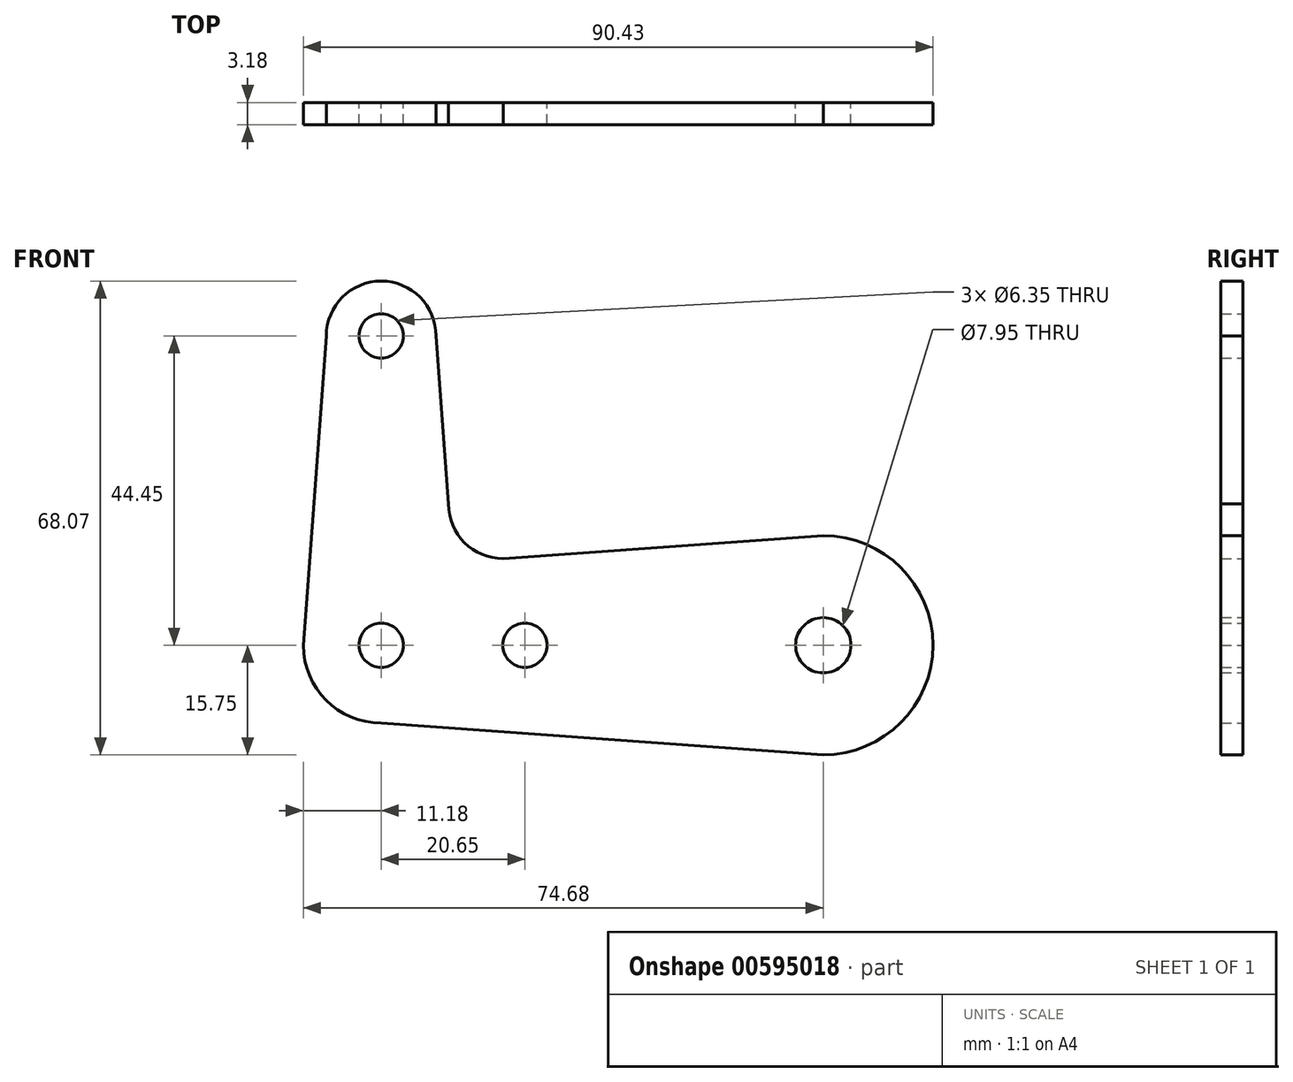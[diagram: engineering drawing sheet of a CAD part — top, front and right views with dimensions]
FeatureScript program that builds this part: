
annotation { "Feature Type Name" : "Feature", "Feature Type Description" : "" }
export const myFeature = defineFeature(function(context is Context, id is Id, definition is map)
    precondition{}
    {
        {
            var Q0;
            Q0=qCreatedBy(makeId("Front.planeOp"),FACE);
            var sketch = newSketch(context, id + "F0", { "sketchPlane" : qUnion([Q0])});
            skLineSegment(sketch, "E0", {"start": v(-20.65, 0) * mm, "end": v(42.85, 0) * mm, "construction": true});
            skLineSegment(sketch, "E1", {"start": v(-20.65, 44.45) * mm, "end": v(-20.65, 0) * mm, "construction": true});
            skCircle(sketch, "E2", {"center": v(-20.65, 0) * mm, "radius": 3.18 * mm});
            skCircle(sketch, "E3", {"center": v(0, 0) * mm, "radius": 3.18 * mm});
            skCircle(sketch, "E4", {"center": v(42.85, 0) * mm, "radius": 3.98 * mm});
            skCircle(sketch, "E5", {"center": v(-20.65, 44.45) * mm, "radius": 3.18 * mm});
            skLineSegment(sketch, "E6", {"start": v(-28.52, 44.45) * mm, "end": v(-31.83, 0) * mm});
            skArc(sketch, "E7", {"start": v(-12.78, 44.45) * mm, "mid": v(-20.65, 52.32) * mm, "end": v(-28.52, 44.45) * mm});
            skArc(sketch, "E8", {"start": v(42.85, -15.75) * mm, "mid": v(58.6, 0) * mm, "end": v(42.85, 15.75) * mm});
            skArc(sketch, "E9", {"start": v(-31.83, 0) * mm, "mid": v(-28.55, -7.9) * mm, "end": v(-20.65, -11.18) * mm});
            skLineSegment(sketch, "E10", {"start": v(-20.65, -11.18) * mm, "end": v(42.85, -15.75) * mm});
            skLineSegment(sketch, "E11", {"start": v(-12.78, 44.45) * mm, "end": v(-10.98, 20.31) * mm});
            skArc(sketch, "E12", {"start": v(-10.98, 20.31) * mm, "mid": v(-8.68, 14.75) * mm, "end": v(-3.1, 12.44) * mm});
            skLineSegment(sketch, "E13", {"start": v(-3.1, 12.44) * mm, "end": v(42.85, 15.75) * mm});
            skSolve(sketch);
        }
        {
            var Q0;
            Q0 = qSketchRegion(id + "F0", true);
            extrude(context, id + "F1", {"entities" : qUnion([Q0]), "depth" : 3.17 * mm, "offsetDistance" : 25.4 * mm});
        }
    });
